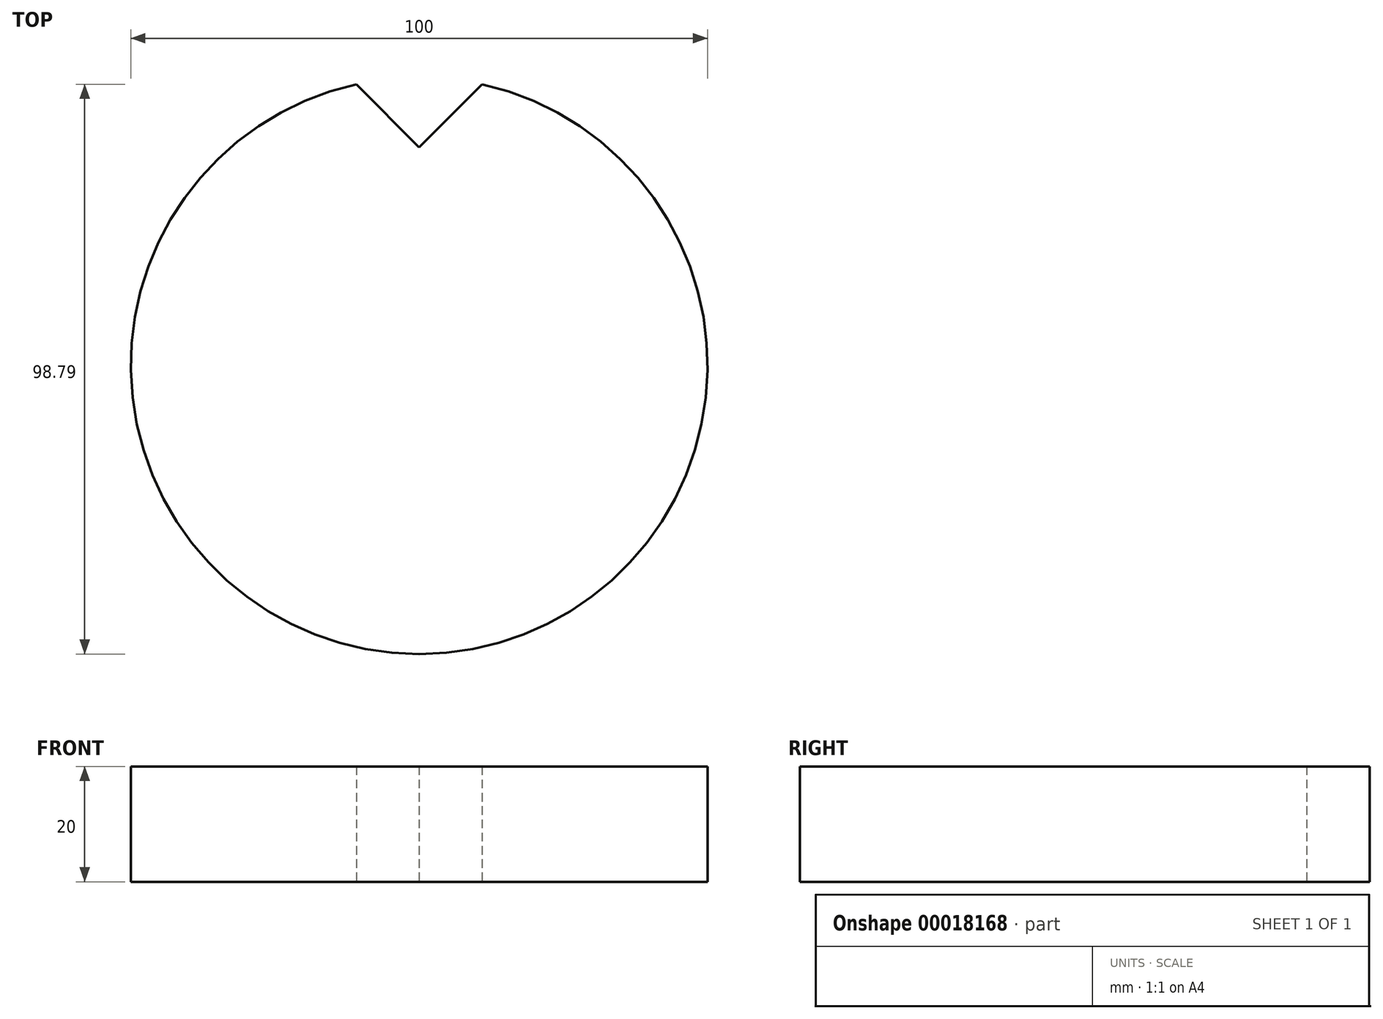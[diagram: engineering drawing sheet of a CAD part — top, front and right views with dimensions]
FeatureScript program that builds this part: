
annotation { "Feature Type Name" : "Feature", "Feature Type Description" : "" }
export const myFeature = defineFeature(function(context is Context, id is Id, definition is map)
    precondition{}
    {
        {
            var Q0;
            Q0=qCreatedBy(makeId("Top.planeOp"),FACE);
            var sketch = newSketch(context, id + "F0", { "sketchPlane" : qUnion([Q0])});
            skArc(sketch, "E0", {"start": v(-10.92, 48.8) * mm, "mid": v(0, -50) * mm, "end": v(10.92, 48.8) * mm});
            skLineSegment(sketch, "E1", {"start": v(-10.92, 48.8) * mm, "end": v(0, 37.88) * mm});
            skLineSegment(sketch, "E2", {"start": v(0, 37.88) * mm, "end": v(10.92, 48.8) * mm});
            skSolve(sketch);
        }
        {
            var Q0;
            Q0=makeQuery(id+"F0.imprint","IMPRINT",FACE,{"disambiguationData":[TD([[makeQuery(id+"F0.imprint","IMPRINT",EDGE,{"derivedFrom":sQuery(id+"F0.wireOp",EDGE,"E0")}),1.0]])]});
            extrude(context, id + "F1", {"entities" : qUnion([Q0]), "depth" : 20 * mm});
        }
    });
